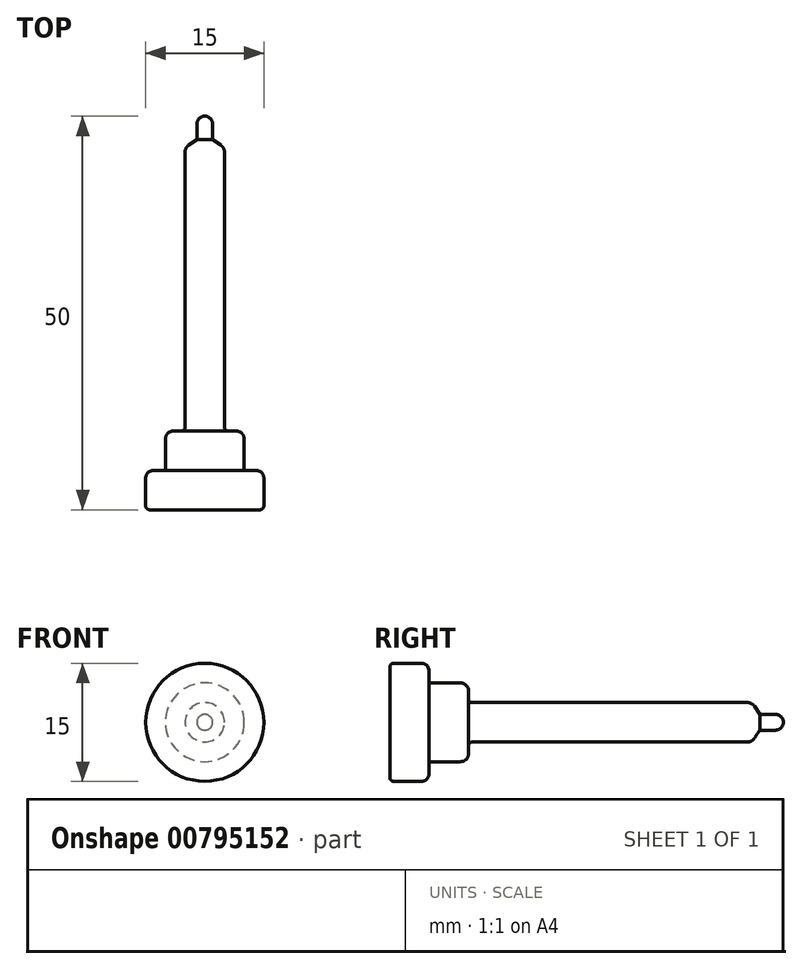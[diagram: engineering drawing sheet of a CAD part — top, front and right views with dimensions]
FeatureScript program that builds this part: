
annotation { "Feature Type Name" : "Feature", "Feature Type Description" : "" }
export const myFeature = defineFeature(function(context is Context, id is Id, definition is map)
    precondition{}
    {
        {
            var Q0;
            Q0=qCreatedBy(makeId("Right.planeOp"),FACE);
            var sketch = newSketch(context, id + "F0", { "sketchPlane" : qUnion([Q0])});
            skLineSegment(sketch, "E0", {"start": v(0, 0) * mm, "end": v(50, 0) * mm});
            skLineSegment(sketch, "E1", {"start": v(50, 0) * mm, "end": v(50, 0) * mm});
            skLineSegment(sketch, "E2", {"start": v(49, 1) * mm, "end": v(47, 1) * mm});
            skLineSegment(sketch, "E3", {"start": v(47, 1) * mm, "end": v(46.3, 2.05) * mm});
            skLineSegment(sketch, "E4", {"start": v(45.46, 2.5) * mm, "end": v(10.5, 2.5) * mm});
            skLineSegment(sketch, "E5", {"start": v(10, 3) * mm, "end": v(10, 4) * mm});
            skLineSegment(sketch, "E6", {"start": v(9, 5) * mm, "end": v(5.25, 5) * mm});
            skLineSegment(sketch, "E7", {"start": v(5, 5.25) * mm, "end": v(5, 6.5) * mm});
            skLineSegment(sketch, "E8", {"start": v(4, 7.5) * mm, "end": v(0.5, 7.5) * mm});
            skLineSegment(sketch, "E9", {"start": v(0, 7) * mm, "end": v(0, 0) * mm});
            skPoint(sketch, "E10.visualSharp", {"position": v(50, 1) * mm});
            skArc(sketch, "E10.filletArc", {"start": v(50, 0) * mm, "mid": v(49.7, 0.7) * mm, "end": v(49, 1) * mm});
            skPoint(sketch, "E11.visualSharp", {"position": v(46, 2.5) * mm});
            skArc(sketch, "E11.filletArc", {"start": v(46.3, 2.05) * mm, "mid": v(45.94, 2.38) * mm, "end": v(45.46, 2.5) * mm});
            skPoint(sketch, "E12.visualSharp", {"position": v(10, 5) * mm});
            skArc(sketch, "E12.filletArc", {"start": v(10, 4) * mm, "mid": v(9.7, 4.7) * mm, "end": v(9, 5) * mm});
            skPoint(sketch, "E13.visualSharp", {"position": v(10, 2.5) * mm});
            skArc(sketch, "E13.filletArc", {"start": v(10, 3) * mm, "mid": v(10.15, 2.65) * mm, "end": v(10.5, 2.5) * mm});
            skPoint(sketch, "E14.visualSharp", {"position": v(5, 5) * mm});
            skArc(sketch, "E14.filletArc", {"start": v(5, 5.25) * mm, "mid": v(5.07, 5.07) * mm, "end": v(5.25, 5) * mm});
            skPoint(sketch, "E15.visualSharp", {"position": v(5, 7.5) * mm});
            skArc(sketch, "E15.filletArc", {"start": v(5, 6.5) * mm, "mid": v(4.7, 7.2) * mm, "end": v(4, 7.5) * mm});
            skPoint(sketch, "E16.visualSharp", {"position": v(0, 7.5) * mm});
            skArc(sketch, "E16.filletArc", {"start": v(0.5, 7.5) * mm, "mid": v(0.15, 7.35) * mm, "end": v(0, 7) * mm});
            skSolve(sketch);
        }
        {
            var Q0;
            Q0=makeQuery(id+"F0.imprint","IMPRINT",FACE,{"disambiguationData":[TD([[makeQuery(id+"F0.imprint","IMPRINT",EDGE,{"derivedFrom":sQuery(id+"F0.wireOp",EDGE,"E0")}),1.0]])]});
            var Q1;
            Q1=sQuery(id+"F0.wireOp",EDGE,"E0");
            revolve(context, id + "F1", {"surfaceOperationType" : NewSurfaceOperationType.NEW, "entities" : qUnion([Q0]), "axis" : qUnion([Q1]), "revolveType" : RevolveType.FULL});
        }
    });
